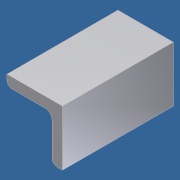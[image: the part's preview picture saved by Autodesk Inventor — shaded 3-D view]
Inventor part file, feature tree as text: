
AUTODESK INVENTOR PART (.ipt)
format: ipt  version: 2012 (Build 160160000, 160)  size: 79,872 bytes
history: native  units: in
note: dims shown in document units (in); Inventor stores cm internally (conversion verified against a paired STEP export)
features: extrude x1, sketch x1
ambient origin geometry x8: Origin, YZ Plane, XZ Plane, XY Plane, X Axis, Y Axis, Z Axis, Center Point
bodies: Solid1 (feature_tree)
feature tree (2):
  extrude  "Extrusion1"  Depth=0.1875in
  sketch  "Sketch1"  dims[d2=1.0in d3=0.1875in d4=0.125in d5=0.094in d6=2.0in d7=0.0in]
